# Revit family: Bticino-Door Entry System-IP-Guard station
name_source: partatom
category: Equipement électrique
units: mm (PartAtom-declared; Revit-internal decimal feet)

## family parameters
Basée sur le plan de construction = Non
Configuration du panneau = Deux colonnes, circuits au sein
Cote de connecteur circulaire = Utiliser le diamètre
Couper avec des vides une fois chargée = Non
Partagée = Non
Point de calcul de pièce = Non
Toujours verticalement = Oui
Type d'élément = Tableau de raccordement

## types (1)
- IP - GUARD STATION
    Configurator website = https://www.homesystems-legrandgroup.com
    Connection type = Network technology
    Depth = 170 mm  [stored 0.557743 ft]
    Elévation par défaut = 0 mm  [stored 0 ft]
    Fabricant = BTICINO
    General Conditions of Use = https://export.legrand.com
    Height = 211 mm
    IP = 30
    Installation method = Desk type device
    Interface type = Full-duplex
    Operating temperature MIN-MAX = -10/+55 °C
    Product designation = IP - GUARD STATION
    Reference = BT-375000
    Tension = 24 V DC
    Touchscreen = Oui
    Width = 308 mm

note: [stored X ft] marks values corroborated as IEEE doubles in the binary element streams (Revit-internal decimal feet)
